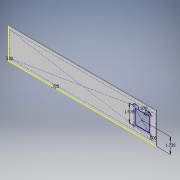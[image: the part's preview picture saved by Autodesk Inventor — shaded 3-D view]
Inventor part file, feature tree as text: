
AUTODESK INVENTOR PART (.ipt)
format: ipt  version: 2017 (Build 210142000, 142)  size: 119,808 bytes
history: native  units: in
note: dims shown in document units (in); Inventor stores cm internally (conversion verified against a paired STEP export)
features: extrude x2, other x1, hole x1, sketch x1
ambient origin geometry x8: Origin, YZ Plane, XZ Plane, XY Plane, X Axis, Y Axis, Z Axis, Center Point
bodies: Solid1 (feature_tree)
feature tree (5):
  extrude  "Extrusion1"  Depth=3.47in
  other  "airflow"
  hole  "Hole1"  [1 undecoded]
  extrude  "Extrusion3"  Depth=0.065in
  sketch  "Sketch1"  dims[d0=16.73in d1=3.47in d2=0.065in d3=0.0in d4=1.97in d5=1.97in d10=1.735in d11=0.325in d12=0.12in d13=0.5in d14=0.155in d15=0.201in d16=0.75in d17=0.385in d18=0.25in d19=0.5635in d20=1.0in d21=0.8108in d22=1.0in d23=0.0in]
note: 1 required parameter value undecoded (feature->parameter linkage not recoverable at this tier; creation-order binding heuristic only, values carry confidence <= 0.55)
